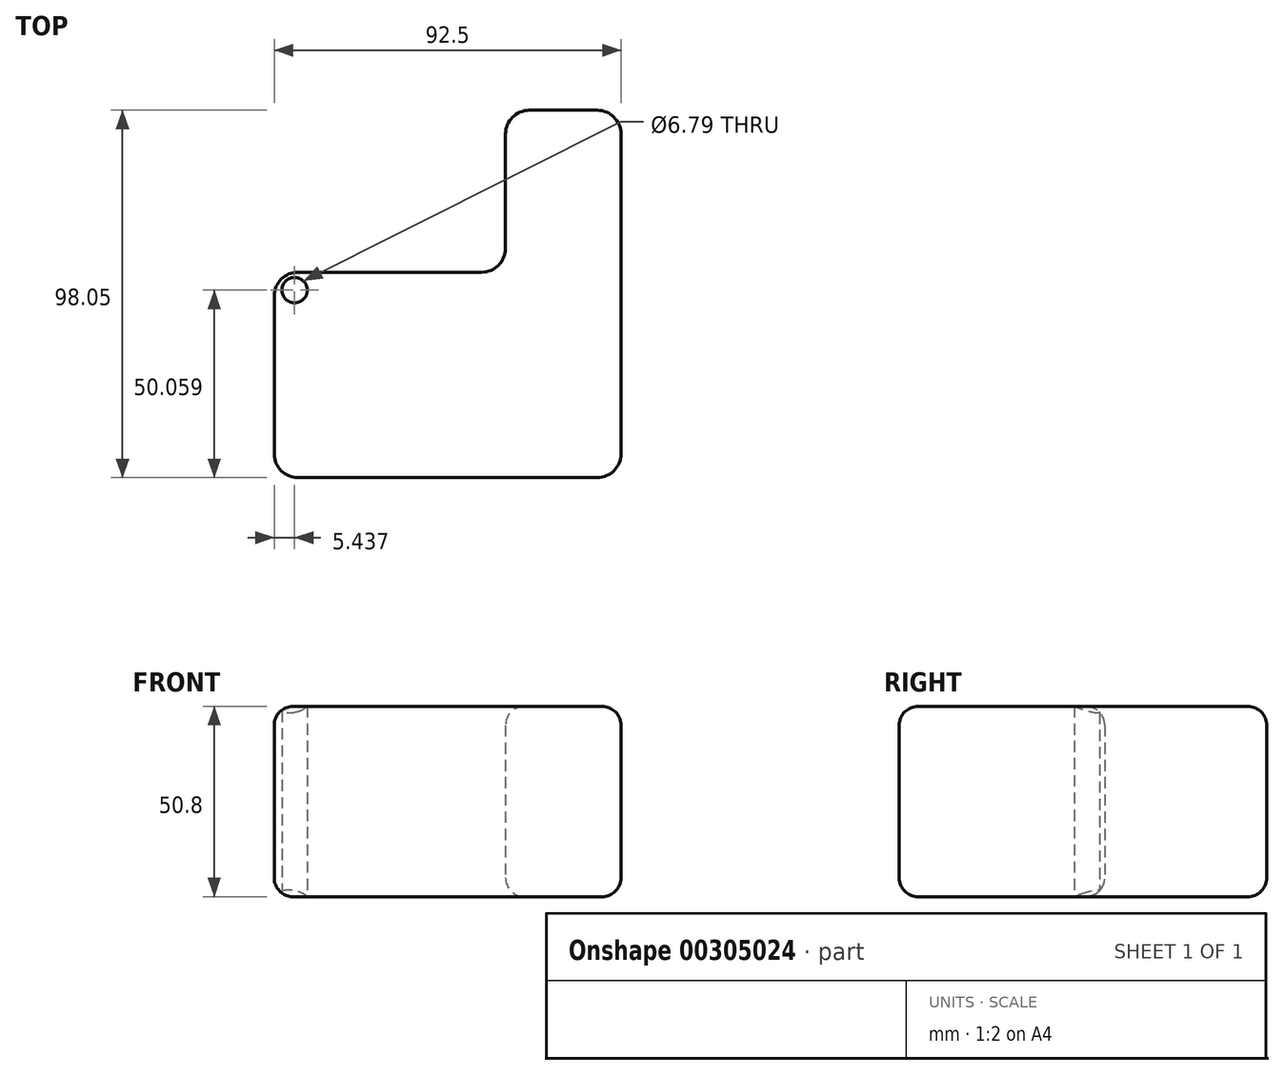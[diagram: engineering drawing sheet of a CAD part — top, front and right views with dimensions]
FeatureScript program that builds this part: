
annotation { "Feature Type Name" : "Feature", "Feature Type Description" : "" }
export const myFeature = defineFeature(function(context is Context, id is Id, definition is map)
    precondition{}
    {
        {
            var Q0;
            Q0=qCreatedBy(makeId("Top.planeOp"),FACE);
            var sketch = newSketch(context, id + "F0", { "sketchPlane" : qUnion([Q0])});
            skLineSegment(sketch, "E0.bottom", {"start": v(-36.02, 20.25) * mm, "end": v(12.99, 20.25) * mm});
            skLineSegment(sketch, "E0.top", {"start": v(-36.02, -34.6) * mm, "end": v(43.78, -34.6) * mm});
            skLineSegment(sketch, "E0.left", {"start": v(-42.37, 13.9) * mm, "end": v(-42.37, -28.25) * mm});
            skLineSegment(sketch, "E0.right", {"start": v(50.13, 20.25) * mm, "end": v(50.13, -28.25) * mm});
            skCircle(sketch, "E1", {"center": v(-36.93, 15.46) * mm, "radius": 3.4 * mm});
            skLineSegment(sketch, "E2.top", {"start": v(43.78, 63.45) * mm, "end": v(25.69, 63.45) * mm});
            skLineSegment(sketch, "E2.left", {"start": v(50.13, 20.25) * mm, "end": v(50.13, 57.1) * mm});
            skLineSegment(sketch, "E2.right", {"start": v(19.34, 26.6) * mm, "end": v(19.34, 57.1) * mm});
            skPoint(sketch, "E3.visualSharp", {"position": v(-42.37, 20.25) * mm});
            skArc(sketch, "E3.filletArc", {"start": v(-36.02, 20.25) * mm, "mid": v(-40.5, 18.39) * mm, "end": v(-42.37, 13.9) * mm});
            skPoint(sketch, "E4.visualSharp", {"position": v(-42.37, -34.6) * mm});
            skArc(sketch, "E4.filletArc", {"start": v(-42.37, -28.25) * mm, "mid": v(-40.5, -32.74) * mm, "end": v(-36.02, -34.6) * mm});
            skPoint(sketch, "E5.visualSharp", {"position": v(50.13, -34.6) * mm});
            skArc(sketch, "E5.filletArc", {"start": v(43.78, -34.6) * mm, "mid": v(48.27, -32.74) * mm, "end": v(50.13, -28.25) * mm});
            skPoint(sketch, "E6.visualSharp", {"position": v(19.34, 20.25) * mm});
            skArc(sketch, "E6.filletArc", {"start": v(12.99, 20.25) * mm, "mid": v(17.48, 22.1) * mm, "end": v(19.34, 26.6) * mm});
            skPoint(sketch, "E7.visualSharp", {"position": v(19.34, 63.45) * mm});
            skArc(sketch, "E7.filletArc", {"start": v(25.69, 63.45) * mm, "mid": v(21.2, 61.6) * mm, "end": v(19.34, 57.1) * mm});
            skPoint(sketch, "E8.visualSharp", {"position": v(50.13, 63.45) * mm});
            skArc(sketch, "E8.filletArc", {"start": v(50.13, 57.1) * mm, "mid": v(48.27, 61.6) * mm, "end": v(43.78, 63.45) * mm});
            skSolve(sketch);
        }
        {
            var Q0;
            Q0 = qSketchRegion(id + "F0", true);
            extrude(context, id + "F1", {"entities" : qUnion([Q0]), "depth" : 50.8 * mm});
        }
        {
            var Q0;
            Q0=makeQuery(id+"F1.opExtrude","CAP_EDGE",EDGE,{"disambiguationData":[OSD([sQuery(id+"F0.wireOp",EDGE,"E0.top")])],"isStart":false});
            var Q1;
            Q1=makeQuery(id+"F1.opExtrude","CAP_EDGE",EDGE,{"disambiguationData":[OSD([sQuery(id+"F0.wireOp",EDGE,"E0.top")])],"isStart":true});
            fillet(context, id + "F2", {"entities" : qUnion([Q0, Q1]), "radius" : 5.08 * mm, "tangentPropagation" : true, "allowEdgeOverflow" : false});
        }
    });
